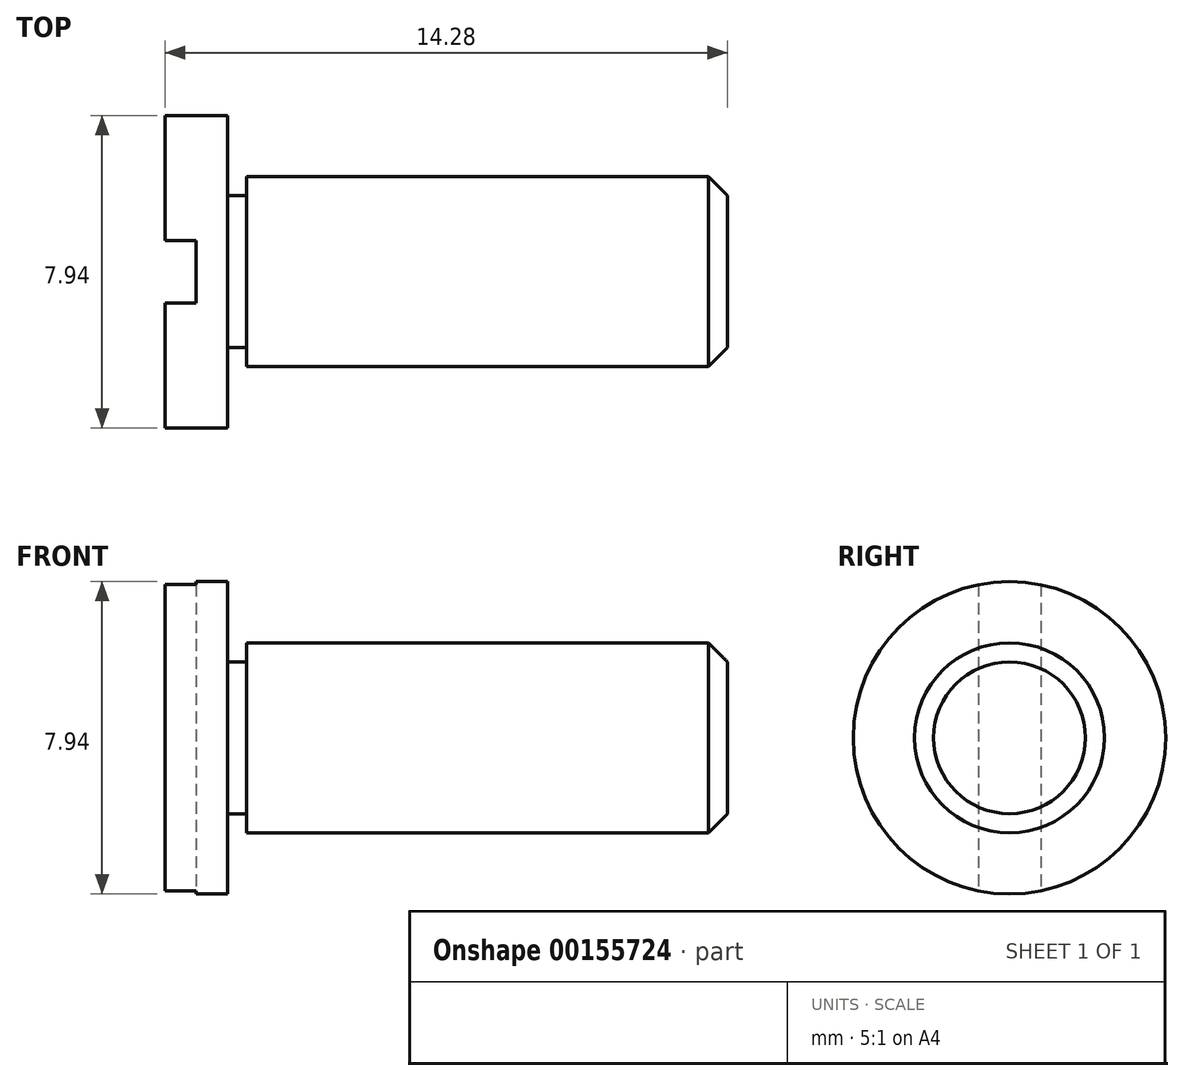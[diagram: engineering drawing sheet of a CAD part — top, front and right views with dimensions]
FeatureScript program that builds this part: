
annotation { "Feature Type Name" : "Feature", "Feature Type Description" : "" }
export const myFeature = defineFeature(function(context is Context, id is Id, definition is map)
    precondition{}
    {
        {
            var Q0;
            Q0=qCreatedBy(makeId("Front.planeOp"),FACE);
            var sketch = newSketch(context, id + "F1", { "sketchPlane" : qUnion([Q0])});
            skLineSegment(sketch, "E0", {"start": v(-7.14, 0) * mm, "end": v(7.14, 0) * mm});
            skLineSegment(sketch, "E1", {"start": v(7.14, 0) * mm, "end": v(7.14, 1.93) * mm});
            skLineSegment(sketch, "E2", {"start": v(7.14, 1.93) * mm, "end": v(6.66, 2.41) * mm});
            skLineSegment(sketch, "E3", {"start": v(6.66, 2.41) * mm, "end": v(-5.07, 2.41) * mm});
            skLineSegment(sketch, "E4", {"start": v(-5.56, 1.93) * mm, "end": v(-5.56, 3.97) * mm});
            skLineSegment(sketch, "E5", {"start": v(-5.56, 3.97) * mm, "end": v(-7.14, 3.97) * mm});
            skLineSegment(sketch, "E6", {"start": v(-7.14, 3.97) * mm, "end": v(-7.14, 0) * mm});
            skLineSegment(sketch, "E7", {"start": v(-5.07, 2.41) * mm, "end": v(-5.07, 1.93) * mm});
            skLineSegment(sketch, "E8", {"start": v(-5.07, 1.93) * mm, "end": v(-5.56, 1.93) * mm});
            skSolve(sketch);
        }
        {
            var Q0;
            Q0 = qSketchRegion(id + "F1", true);
            var Q1;
            Q1=sQuery(id+"F1.wireOp",EDGE,"E0");
            revolve(context, id + "F0", {"entities" : qUnion([Q0]), "axis" : qUnion([Q1]), "revolveType" : RevolveType.FULL});
        }
        {
            var Q0;
            Q0=makeQuery(id+"F0.opRevolve","SWEPT_FACE",FACE,{"disambiguationData":[OSD([sQuery(id+"F1.wireOp",EDGE,"E6")])]});
            var sketch = newSketch(context, id + "F2", { "sketchPlane" : qUnion([Q0])});
            skLineSegment(sketch, "E9.bottom", {"start": v(-0.8, 3.97) * mm, "end": v(0.8, 3.97) * mm});
            skLineSegment(sketch, "E9.top", {"start": v(-0.8, -3.97) * mm, "end": v(0.8, -3.97) * mm});
            skLineSegment(sketch, "E9.left", {"start": v(-0.8, 3.97) * mm, "end": v(-0.8, -3.97) * mm});
            skLineSegment(sketch, "E9.right", {"start": v(0.8, 3.97) * mm, "end": v(0.8, -3.97) * mm});
            skPoint(sketch, "E9.middle", {"position": v(0, 0) * mm});
            skSolve(sketch);
        }
        {
            var Q0;
            Q0 = qSketchRegion(id + "F2", true);
            extrude(context, id + "F3", {"entities" : qUnion([Q0]), "operationType" : NewBodyOperationType.REMOVE, "oppositeDirection" : true, "depth" : 0.8 * mm});
        }
    });
